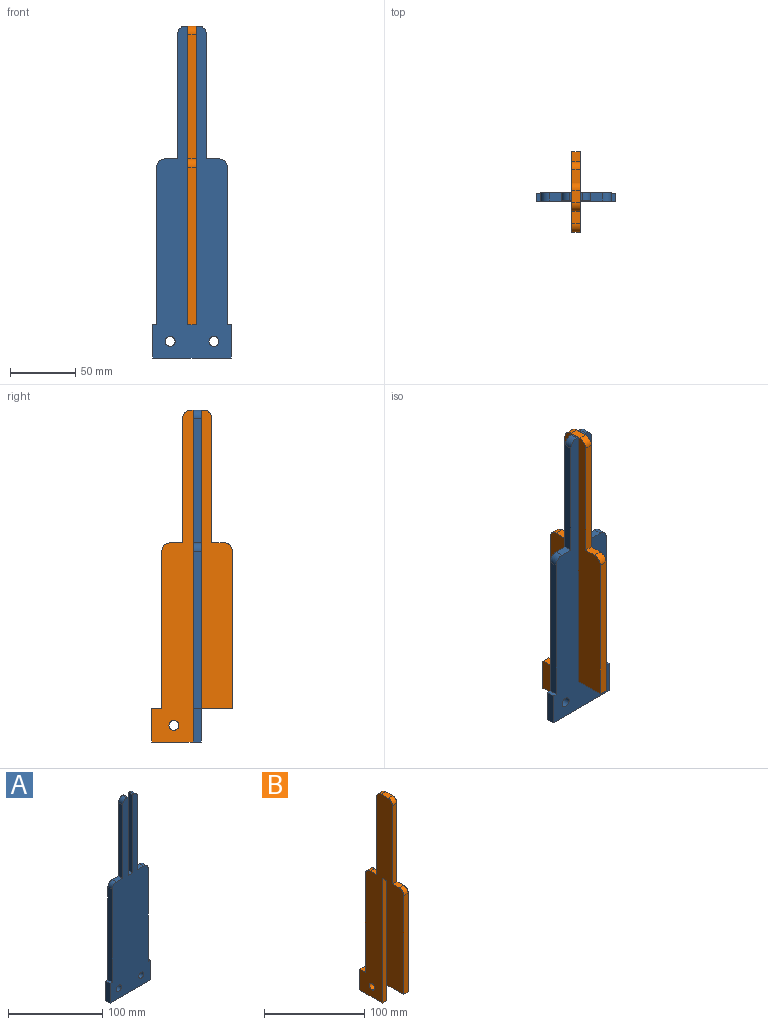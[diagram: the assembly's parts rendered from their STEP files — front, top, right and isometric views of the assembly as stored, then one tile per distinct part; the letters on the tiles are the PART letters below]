
ASSEMBLY  parts=2 mates=1
PART A: 24 faces, bbox 60.3x6.4x254 mm
  f0: plane 60.33x6.35mm, normal (0,0,-1), area 383.1mm2, adj f1,f20,f22,f23
  f1: plane 25.4x6.35mm, normal (1,0,0), area 161.3mm2, adj f0,f2,f22,f23
  f2: plane 6.35x3.18mm, normal (0,0,1), area 20.2mm2, adj f1,f3,f22,f23
  f3: plane 120.65x6.35mm, normal (1,0,0), area 766.1mm2, adj f2,f4,f22,f23
  f4: cylinder r=6.35mm len=6.35mm, axis (0,1,0), area 63.3mm2, adj f3,f5,f22,f23
  f5: plane 9.53x6.35mm, normal (0,0,1), area 60.5mm2, adj f4,f6,f22,f23
  f6: plane 95.25x6.35mm, normal (1,0,0), area 604.8mm2, adj f5,f7,f22,f23
  f7: cylinder r=6.35mm len=6.35mm, axis (0,1,0), area 63.3mm2, adj f6,f8,f22,f23
  f8: plane 6.35x1.55mm, normal (0,0,1), area 9.9mm2, adj f7,f9,f22,f23
  f9: plane 101.6x6.35mm, normal (-1,0,0), area 645.2mm2, adj f8,f10,f22,f23
  f10: plane 6.35x6.31mm, normal (0,0,1), area 40.1mm2, adj f9,f11,f22,f23
  f11: plane 101.6x6.35mm, normal (1,0,0), area 645.2mm2, adj f10,f12,f22,f23
  f12: plane 6.35x1.62mm, normal (0,0,1), area 10.3mm2, adj f11,f13,f22,f23
  f13: cylinder r=6.35mm len=6.35mm, axis (0,1,0), area 63.3mm2, adj f12,f14,f22,f23
  f14: plane 95.25x6.35mm, normal (-1,0,0), area 604.8mm2, adj f13,f15,f22,f23
  f15: plane 9.53x6.35mm, normal (0,0,1), area 60.5mm2, adj f14,f16,f22,f23
  f16: cylinder r=6.35mm len=6.35mm, axis (0,1,0), area 63.3mm2, adj f15,f17,f22,f23
  f17: plane 120.65x6.35mm, normal (-1,0,0), area 766.1mm2, adj f16,f18,f22,f23
  f18: plane 6.35x3.18mm, normal (0,0,1), area 20.2mm2, adj f17,f20,f22,f23
  f19: cylinder r=3.81mm len=7.62mm, axis (0,1,0), area 152mm2, adj f22,f23
  f20: plane 25.4x6.35mm, normal (-1,0,0), area 161.3mm2, adj f0,f18,f22,f23
  f21: cylinder r=3.81mm len=7.62mm, axis (0,1,0), area 152mm2, adj f22,f23
  f22: plane 254x60.33mm, normal (0,-1,0), area 9876mm2, adj f0,f1,f2,f3,f4,f5,f6,f7
  f23: plane 254x60.33mm, normal (0,1,0), area 9876mm2, adj f0,f1,f2,f3,f4,f5,f6,f7
PART B: 21 faces, bbox 6.4x61.9x254 mm
  f0: plane 152.4x6.35mm, normal (0,-1,0), area 967.7mm2, adj f1,f17,f19,f20
  f1: plane 31.75x6.35mm, normal (0,0,-1), area 201.6mm2, adj f0,f2,f19,f20
  f2: plane 25.4x6.35mm, normal (0,1,0), area 161.3mm2, adj f1,f3,f19,f20
  f3: plane 7.94x6.35mm, normal (0,0,1), area 50.4mm2, adj f2,f4,f19,f20
  f4: plane 120.65x6.35mm, normal (0,1,0), area 766.1mm2, adj f3,f5,f19,f20
  f5: cylinder r=6.35mm len=6.35mm, axis (-1,0,0), area 63.3mm2, adj f4,f6,f19,f20
  f6: plane 9.52x6.35mm, normal (0,0,1), area 60.5mm2, adj f5,f7,f19,f20
  f7: plane 95.25x6.35mm, normal (0,1,0), area 604.8mm2, adj f6,f8,f19,f20
  f8: cylinder r=6.35mm len=6.35mm, axis (-1,0,0), area 63.3mm2, adj f7,f9,f19,f20
  f9: plane 9.52x6.35mm, normal (0,0,1), area 60.5mm2, adj f8,f10,f19,f20
  f10: cylinder r=6.35mm len=6.35mm, axis (-1,0,0), area 63.3mm2, adj f9,f11,f19,f20
  f11: plane 95.25x6.35mm, normal (0,-1,0), area 604.8mm2, adj f10,f12,f19,f20
  f12: plane 9.54x6.35mm, normal (0,0,1), area 60.6mm2, adj f11,f13,f19,f20
  f13: cylinder r=6.35mm len=6.35mm, axis (-1,0,0), area 63.3mm2, adj f12,f14,f19,f20
  f14: plane 120.65x6.35mm, normal (0,-1,0), area 766.1mm2, adj f13,f15,f19,f20
  f15: plane 23.81x6.35mm, normal (0,0,-1), area 151.2mm2, adj f14,f16,f19,f20
  f16: plane 127x6.35mm, normal (0,1,0), area 806.5mm2, adj f15,f17,f19,f20
  f17: plane 6.35x6.35mm, normal (0,0,-1), area 40.3mm2, adj f0,f16,f19,f20
  f18: cylinder r=3.81mm len=7.62mm, axis (-1,0,0), area 152mm2, adj f19,f20
  f19: plane 254x61.91mm, normal (1,0,0), area 9032.1mm2, adj f0,f1,f2,f3,f4,f5,f6,f7
  f20: plane 254x61.91mm, normal (-1,0,0), area 9032.1mm2, adj f0,f1,f2,f3,f4,f5,f6,f7
PLACE A t=(10.48,62.18,-24.17)mm
PLACE B t=(10.5,62.18,52.03)mm
MATE fastened A.f10 <-> B.f17  axis (0,0,1) through (10.5,62.18,115.53)mm
